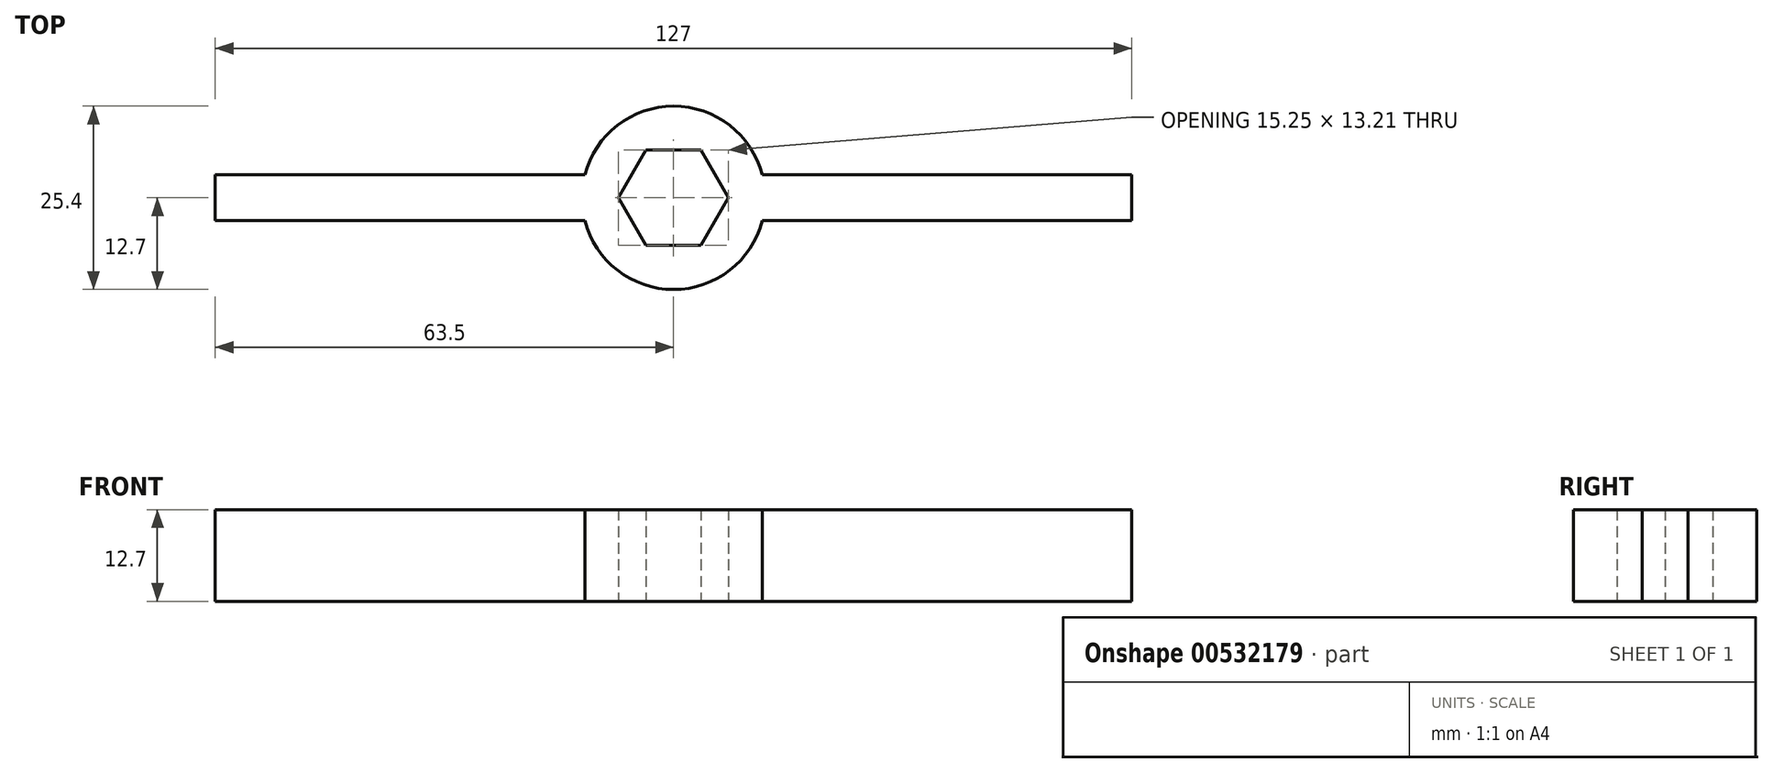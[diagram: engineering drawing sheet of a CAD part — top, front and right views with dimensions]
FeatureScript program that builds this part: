
annotation { "Feature Type Name" : "Feature", "Feature Type Description" : "" }
export const myFeature = defineFeature(function(context is Context, id is Id, definition is map)
    precondition{}
    {
        {
            var Q0;
            Q0=qCreatedBy(makeId("Top.planeOp"),FACE);
            var sketch = newSketch(context, id + "F0", { "sketchPlane" : qUnion([Q0])});
            skCircle(sketch, "E0.cCircle", {"center": v(0, 0) * mm, "radius": 6.6 * mm, "construction": true});
            skLineSegment(sketch, "E0.0", {"start": v(3.81, 6.6) * mm, "end": v(7.63, 0) * mm});
            skLineSegment(sketch, "E0.1", {"start": v(7.63, 0) * mm, "end": v(3.81, -6.6) * mm});
            skLineSegment(sketch, "E0.2", {"start": v(3.81, -6.6) * mm, "end": v(-3.81, -6.6) * mm});
            skLineSegment(sketch, "E0.3", {"start": v(-3.81, -6.6) * mm, "end": v(-7.63, 0) * mm});
            skLineSegment(sketch, "E0.4", {"start": v(-7.63, 0) * mm, "end": v(-3.81, 6.6) * mm});
            skLineSegment(sketch, "E0.5", {"start": v(-3.81, 6.6) * mm, "end": v(3.81, 6.6) * mm});
            skPoint(sketch, "E0.0.midPoint", {"position": v(5.72, 3.3) * mm});
            skPoint(sketch, "E1", {"position": v(0, 6.6) * mm});
            skCircle(sketch, "E2", {"center": v(0, 0) * mm, "radius": 12.7 * mm});
            skLineSegment(sketch, "E3.bottom", {"start": v(0, -3.18) * mm, "end": v(-63.5, -3.17) * mm});
            skLineSegment(sketch, "E3.top", {"start": v(0, 3.17) * mm, "end": v(-63.5, 3.18) * mm});
            skLineSegment(sketch, "E3.left", {"start": v(0, 3.17) * mm, "end": v(0, -3.17) * mm});
            skLineSegment(sketch, "E3.right", {"start": v(-63.5, 3.18) * mm, "end": v(-63.5, -3.18) * mm});
            skLineSegment(sketch, "E4.MirrorCS", {"start": v(0, 3.17) * mm, "end": v(63.5, 3.17) * mm});
            skLineSegment(sketch, "E5.MirrorCS", {"start": v(63.5, 3.18) * mm, "end": v(63.5, -3.17) * mm});
            skLineSegment(sketch, "E6.MirrorCS", {"start": v(0, -3.18) * mm, "end": v(63.5, -3.18) * mm});
            skSolve(sketch);
        }
        {
            var Q0;
            {var subQ5=sQuery(id+"F0.wireOp",EDGE,"E3.right");Q0=makeQuery(id+"F0.imprint","IMPRINT",FACE,{"disambiguationData":[TD([[makeQuery(id+"F0.imprint","IMPRINT",EDGE,{"derivedFrom":subQ5}),1.0]])]});}
            var Q1;
            {var subQ3=sQuery(id+"F0.wireOp",EDGE,"E0.3");var subQ5=sQuery(id+"F0.wireOp",EDGE,"E0.4");var subQ6=makeQuery(id+"F0.imprint","INTERSECT",VERTEX,{"derivedFrom":[subQ3,subQ5]});Q1=makeQuery(id+"F0.imprint","IMPRINT",FACE,{"disambiguationData":[TD([[makeQuery(id+"F0.imprint","IMPRINT",EDGE,{"disambiguationData":[TD([[subQ6,1.0]])],"derivedFrom":subQ3}),1.0]])]});}
            var Q2;
            {var subQ0=sQuery(id+"F0.wireOp",EDGE,"E0.5");Q2=makeQuery(id+"F0.imprint","IMPRINT",FACE,{"disambiguationData":[TD([[makeQuery(id+"F0.imprint","IMPRINT",EDGE,{"derivedFrom":subQ0}),1.0]])]});}
            var Q3;
            {var subQ3=sQuery(id+"F0.wireOp",EDGE,"E0.0");var subQ5=sQuery(id+"F0.wireOp",EDGE,"E0.1");var subQ6=makeQuery(id+"F0.imprint","INTERSECT",VERTEX,{"derivedFrom":[subQ3,subQ5]});Q3=makeQuery(id+"F0.imprint","IMPRINT",FACE,{"disambiguationData":[TD([[makeQuery(id+"F0.imprint","IMPRINT",EDGE,{"disambiguationData":[TD([[subQ6,1.0]])],"derivedFrom":subQ3}),1.0]])]});}
            var Q4;
            {var subQ6=sQuery(id+"F0.wireOp",EDGE,"E0.2");Q4=makeQuery(id+"F0.imprint","IMPRINT",FACE,{"disambiguationData":[TD([[makeQuery(id+"F0.imprint","IMPRINT",EDGE,{"derivedFrom":subQ6}),1.0]])]});}
            var Q5;
            {var subQ5=sQuery(id+"F0.wireOp",EDGE,"E5.MirrorCS");Q5=makeQuery(id+"F0.imprint","IMPRINT",FACE,{"disambiguationData":[TD([[makeQuery(id+"F0.imprint","IMPRINT",EDGE,{"derivedFrom":subQ5}),-1.0]])]});}
            extrude(context, id + "F1", {"entities" : qUnion([Q0, Q1, Q2, Q3, Q4, Q5]), "depth" : 12.7 * mm, "offsetDistance" : 25.4 * mm});
        }
    });
